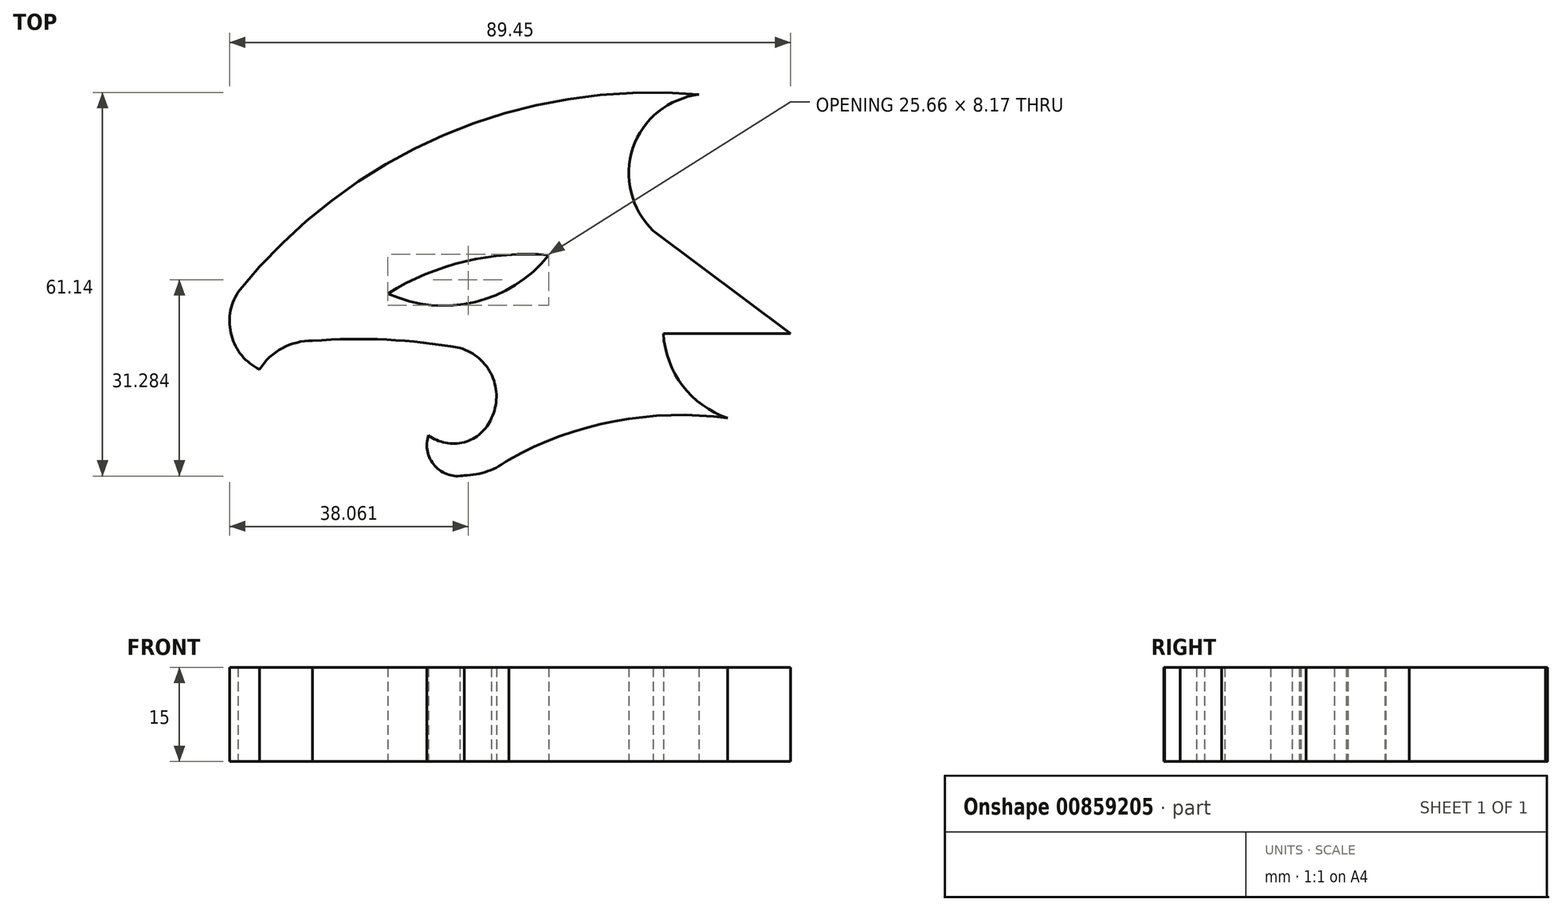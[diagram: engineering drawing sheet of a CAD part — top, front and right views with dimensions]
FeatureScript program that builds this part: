
annotation { "Feature Type Name" : "Feature", "Feature Type Description" : "" }
export const myFeature = defineFeature(function(context is Context, id is Id, definition is map)
    precondition{}
    {
        {
            var Q0;
            Q0=qCreatedBy(makeId("Top.planeOp"),FACE);
            var sketch = newSketch(context, id + "F0", { "sketchPlane" : qUnion([Q0])});
            skArc(sketch, "E0", {"start": v(25.66, 7.78) * mm, "mid": v(12.34, 6.78) * mm, "end": v(0, 1.65) * mm});
            skArc(sketch, "E1", {"start": v(0, 1.65) * mm, "mid": v(13.89, 0.3) * mm, "end": v(25.66, 7.78) * mm});
            skArc(sketch, "E2", {"start": v(-23.86, 1.87) * mm, "mid": v(-24.92, -5.06) * mm, "end": v(-20.43, -10.45) * mm});
            skArc(sketch, "E3", {"start": v(49.61, 33.36) * mm, "mid": v(8.9, 26.9) * mm, "end": v(-23.86, 1.87) * mm});
            skArc(sketch, "E4", {"start": v(49.61, 33.36) * mm, "mid": v(39.07, 24.84) * mm, "end": v(42.31, 11.68) * mm});
            skLineSegment(sketch, "E5", {"start": v(42.31, 11.68) * mm, "end": v(64.22, -4.75) * mm});
            skLineSegment(sketch, "E6", {"start": v(64.22, -4.75) * mm, "end": v(33.41, -4.75) * mm});
            skArc(sketch, "E7", {"start": v(-12, -5.89) * mm, "mid": v(-16.82, -7.05) * mm, "end": v(-20.43, -10.45) * mm});
            skArc(sketch, "E8", {"start": v(11.5, -7.03) * mm, "mid": v(-0.2, -5.7) * mm, "end": v(-12, -5.89) * mm});
            skArc(sketch, "E9", {"start": v(16.53, -18.2) * mm, "mid": v(16.6, -11.46) * mm, "end": v(11.5, -7.03) * mm});
            skArc(sketch, "E10", {"start": v(6.49, -20.95) * mm, "mid": v(12.18, -22.03) * mm, "end": v(16.53, -18.2) * mm});
            skArc(sketch, "E11", {"start": v(6.49, -20.95) * mm, "mid": v(7.48, -25.8) * mm, "end": v(12.18, -27.34) * mm});
            skPoint(sketch, "E11.endSnap0", {"position": v(12.18, -22.03) * mm});
            skArc(sketch, "E12", {"start": v(12.18, -27.34) * mm, "mid": v(15.93, -26.65) * mm, "end": v(19.27, -24.83) * mm});
            skArc(sketch, "E13", {"start": v(54.18, -18.2) * mm, "mid": v(36.19, -18.7) * mm, "end": v(19.27, -24.83) * mm});
            skArc(sketch, "E14", {"start": v(43.91, -4.75) * mm, "mid": v(47, -13.03) * mm, "end": v(54.18, -18.2) * mm});
            skSolve(sketch);
        }
        {
            var Q0;
            Q0=makeQuery(id+"F0.imprint","IMPRINT",FACE,{"disambiguationData":[TD([[makeQuery(id+"F0.imprint","IMPRINT",EDGE,{"derivedFrom":sQuery(id+"F0.wireOp",EDGE,"E0")}),-1.0]])]});
            extrude(context, id + "F1", {"entities" : qUnion([Q0]), "depth" : 15 * mm, "offsetDistance" : 25 * mm});
        }
    });
